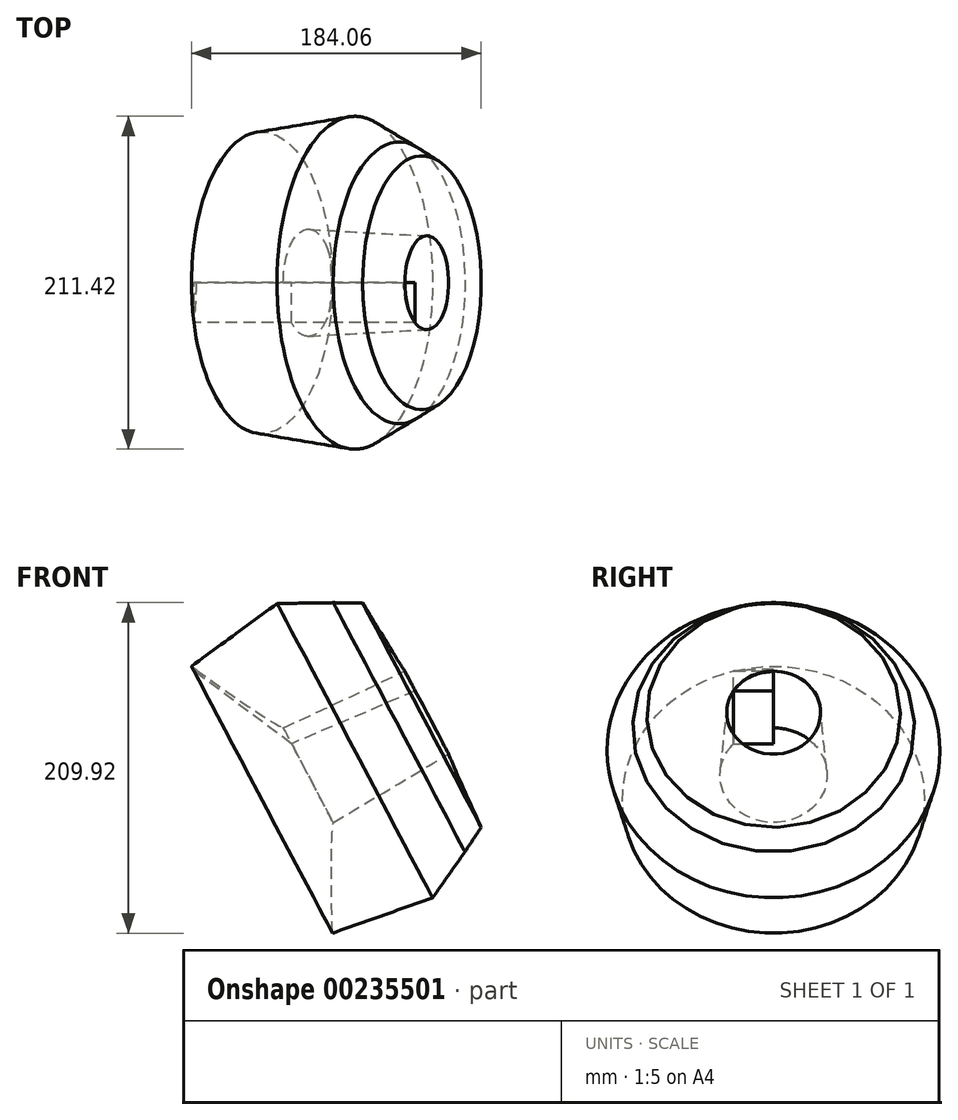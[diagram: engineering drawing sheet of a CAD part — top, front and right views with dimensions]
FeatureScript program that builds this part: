
annotation { "Feature Type Name" : "Feature", "Feature Type Description" : "" }
export const myFeature = defineFeature(function(context is Context, id is Id, definition is map)
    precondition{}
    {
        {
            var Q0;
            Q0=qCreatedBy(makeId("Front.planeOp"),FACE);
            var sketch = newSketch(context, id + "F0", { "sketchPlane" : qUnion([Q0])});
            skLineSegment(sketch, "E0", {"start": v(-62.04, 17.23) * mm, "end": v(-7.8, 57.4) * mm});
            skLineSegment(sketch, "E1", {"start": v(-7.8, 57.4) * mm, "end": v(28.17, 57.4) * mm});
            skLineSegment(sketch, "E2", {"start": v(47.06, 56.8) * mm, "end": v(78.53, 4.65) * mm});
            skLineSegment(sketch, "E3", {"start": v(78.53, 4.65) * mm, "end": v(0, -28.92) * mm});
            skLineSegment(sketch, "E4", {"start": v(0, -28.92) * mm, "end": v(-62.04, 17.23) * mm});
            skLineSegment(sketch, "E5", {"start": v(28.17, 57.4) * mm, "end": v(47.06, 56.8) * mm});
            skSolve(sketch);
        }
        {
            var Q0;
            Q0=makeQuery(id+"F0.imprint","IMPRINT",FACE,{"disambiguationData":[TD([[makeQuery(id+"F0.imprint","IMPRINT",EDGE,{"derivedFrom":sQuery(id+"F0.wireOp",EDGE,"E0")}),-1.0]])]});
            extrude(context, id + "F1", {"entities" : qUnion([Q0]), "depth" : 25.4 * mm});
        }
        {
            var Q0;
            Q0=qCreatedBy(makeId("Front.planeOp"),FACE);
            var sketch = newSketch(context, id + "F2", { "sketchPlane" : qUnion([Q0])});
            skLineSegment(sketch, "E6", {"start": v(15.59, -46.3) * mm, "end": v(84.22, -10.04) * mm});
            skSolve(sketch);
        }
        {
            var Q0;
            Q0=makeQuery(id+"F1.opExtrude","CAP_FACE",FACE,{"disambiguationData":[OSD([sQuery(id+"F0.wireOp",EDGE,"E0"),sQuery(id+"F0.wireOp",EDGE,"E1"),sQuery(id+"F0.wireOp",EDGE,"E2"),sQuery(id+"F0.wireOp",EDGE,"E3"),sQuery(id+"F0.wireOp",EDGE,"E4"),sQuery(id+"F0.wireOp",EDGE,"E5")])],"isStart":false});
            var Q1;
            Q1=sQuery(id+"F2.wireOp",EDGE,"E6");
            revolve(context, id + "F3", {"operationType" : NewBodyOperationType.ADD, "entities" : qUnion([Q0]), "axis" : qUnion([Q1]), "revolveType" : RevolveType.FULL});
        }
    });
